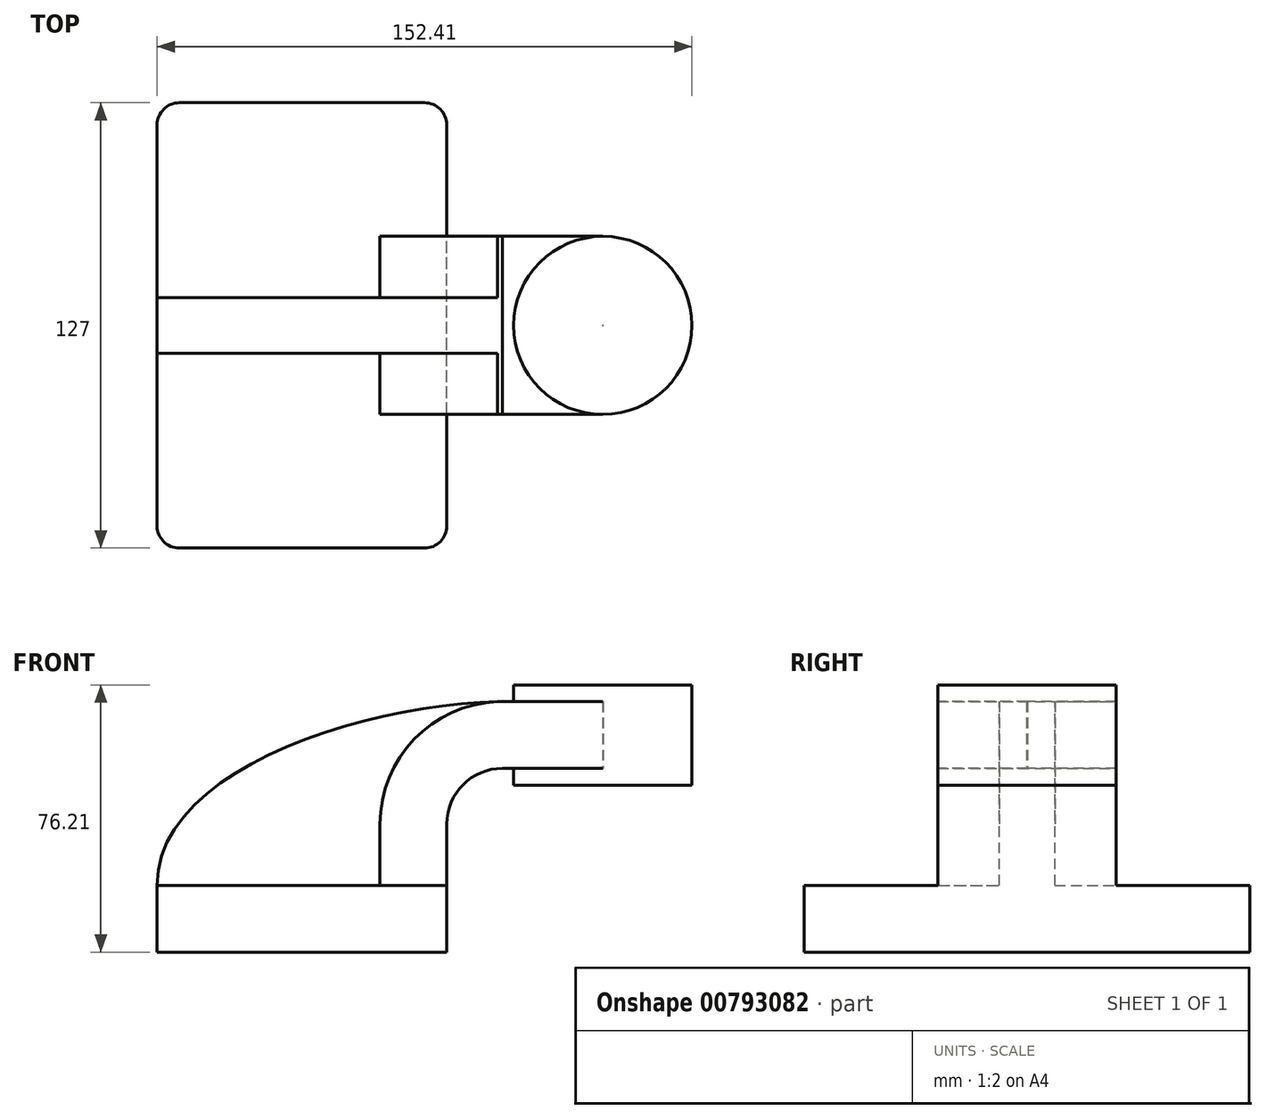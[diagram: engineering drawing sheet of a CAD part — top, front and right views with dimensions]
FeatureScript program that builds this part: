
annotation { "Feature Type Name" : "Feature", "Feature Type Description" : "" }
export const myFeature = defineFeature(function(context is Context, id is Id, definition is map)
    precondition{}
    {
        {
            var Q0;
            Q0=qCreatedBy(makeId("Front.planeOp"),FACE);
            var sketch = newSketch(context, id + "F0", { "sketchPlane" : qUnion([Q0])});
            skLineSegment(sketch, "E0.bottom", {"start": v(-41.28, 9.52) * mm, "end": v(41.27, 9.53) * mm});
            skLineSegment(sketch, "E0.top", {"start": v(-41.28, -9.52) * mm, "end": v(41.28, -9.52) * mm});
            skLineSegment(sketch, "E0.left", {"start": v(-41.28, 9.52) * mm, "end": v(-41.28, -9.53) * mm});
            skLineSegment(sketch, "E0.right", {"start": v(41.27, 9.53) * mm, "end": v(41.28, -9.52) * mm});
            skPoint(sketch, "E0.middle", {"position": v(0, 0) * mm});
            skLineSegment(sketch, "E1.bottom", {"start": v(60.32, 38.1) * mm, "end": v(111.12, 38.1) * mm});
            skLineSegment(sketch, "E1.top", {"start": v(60.32, 66.67) * mm, "end": v(111.12, 66.67) * mm});
            skLineSegment(sketch, "E1.left", {"start": v(60.32, 38.1) * mm, "end": v(60.32, 66.67) * mm});
            skLineSegment(sketch, "E1.right", {"start": v(111.12, 38.1) * mm, "end": v(111.12, 66.67) * mm});
            skPoint(sketch, "E1.middle", {"position": v(85.72, 52.39) * mm});
            skLineSegment(sketch, "E2", {"start": v(41.27, 9.53) * mm, "end": v(41.27, 27) * mm});
            skArc(sketch, "E3", {"start": v(41.27, 27) * mm, "mid": v(45.92, 38.23) * mm, "end": v(57.15, 42.88) * mm});
            skLineSegment(sketch, "E4", {"start": v(57.15, 42.88) * mm, "end": v(85.82, 42.88) * mm});
            skLineSegment(sketch, "E5.0", {"start": v(57.15, 61.93) * mm, "end": v(85.82, 61.93) * mm});
            skArc(sketch, "E5.1", {"start": v(22.22, 27) * mm, "mid": v(32.45, 51.7) * mm, "end": v(57.15, 61.93) * mm});
            skLineSegment(sketch, "E5.2", {"start": v(22.22, 9.53) * mm, "end": v(22.22, 27) * mm});
            skFitSpline(sketch, "E6", {"points": [v(-41.28, 9.52) * mm, v(57.15, 61.93) * mm], "startDerivative": vector(-0.22, 101.04) * mm, "endDerivative": vector(113.45, 1.62) * mm});
            skLineSegment(sketch, "E7", {"start": v(85.82, 42.88) * mm, "end": v(85.82, 61.93) * mm});
            skLineSegment(sketch, "E8", {"start": v(85.72, 38.1) * mm, "end": v(85.72, 66.67) * mm});
            skSolve(sketch);
        }
        {
            var Q0;
            Q0=makeQuery(id+"F0.imprint","IMPRINT",FACE,{"disambiguationData":[TD([[makeQuery(id+"F0.imprint","IMPRINT",EDGE,{"derivedFrom":sQuery(id+"F0.wireOp",EDGE,"E0.top")}),1.0]])]});
            extrude(context, id + "F1", {"entities" : qUnion([Q0]), "endBound" : BoundingType.SYMMETRIC, "depth" : 127 * mm, "offsetDistance" : 25.4 * mm});
        }
        {
            var Q0;
            {var subQ6=sQuery(id+"F0.wireOp",EDGE,"E2");Q0=makeQuery(id+"F0.imprint","IMPRINT",FACE,{"disambiguationData":[TD([[makeQuery(id+"F0.imprint","IMPRINT",EDGE,{"derivedFrom":subQ6}),1.0]])]});}
            var Q1;
            {var subQ0=sQuery(id+"F0.wireOp",EDGE,"E4");var subQ1=sQuery(id+"F0.wireOp",EDGE,"E1.left");var subQ2=makeQuery(id+"F0.imprint","INTERSECT",VERTEX,{"derivedFrom":[subQ1,subQ0]});Q1=makeQuery(id+"F0.imprint","IMPRINT",FACE,{"disambiguationData":[TD([[makeQuery(id+"F0.imprint","IMPRINT",EDGE,{"disambiguationData":[TD([[subQ2,-1.0]])],"derivedFrom":subQ1}),-1.0]])]});}
            extrude(context, id + "F2", {"entities" : qUnion([Q0, Q1]), "operationType" : NewBodyOperationType.ADD, "endBound" : BoundingType.SYMMETRIC, "depth" : 50.8 * mm, "offsetDistance" : 25.4 * mm});
        }
        {
            var Q0;
            {var subQ3=sQuery(id+"F0.wireOp",EDGE,"E5.2");Q0=makeQuery(id+"F0.imprint","IMPRINT",FACE,{"disambiguationData":[TD([[makeQuery(id+"F0.imprint","IMPRINT",EDGE,{"derivedFrom":subQ3}),1.0]])]});}
            extrude(context, id + "F3", {"entities" : qUnion([Q0]), "operationType" : NewBodyOperationType.ADD, "endBound" : BoundingType.SYMMETRIC, "depth" : 15.88 * mm, "offsetDistance" : 25.4 * mm});
        }
        {
            var Q0;
            {var subQ4=sQuery(id+"F0.wireOp",EDGE,"E1.right");Q0=makeQuery(id+"F0.imprint","IMPRINT",FACE,{"disambiguationData":[TD([[makeQuery(id+"F0.imprint","IMPRINT",EDGE,{"derivedFrom":subQ4}),1.0]])]});}
            var Q1;
            Q1=sQuery(id+"F0.wireOp",EDGE,"E8");
            revolve(context, id + "F4", {"operationType" : NewBodyOperationType.ADD, "surfaceOperationType" : NewSurfaceOperationType.NEW, "entities" : qUnion([Q0]), "axis" : qUnion([Q1]), "revolveType" : RevolveType.FULL});
        }
        {
            var Q0;
            Q0=makeQuery(id+"F1.opExtrude","CAP_EDGE",EDGE,{"disambiguationData":[OSD([sQuery(id+"F0.wireOp",EDGE,"E0.left")])],"isStart":false});
            var Q1;
            Q1=makeQuery(id+"F1.opExtrude","CAP_EDGE",EDGE,{"disambiguationData":[OSD([sQuery(id+"F0.wireOp",EDGE,"E0.right")])],"isStart":false});
            var Q2;
            Q2=makeQuery(id+"F1.opExtrude","CAP_EDGE",EDGE,{"disambiguationData":[OSD([sQuery(id+"F0.wireOp",EDGE,"E0.left")])],"isStart":true});
            var Q3;
            Q3=makeQuery(id+"F1.opExtrude","CAP_EDGE",EDGE,{"disambiguationData":[OSD([sQuery(id+"F0.wireOp",EDGE,"E0.right")])],"isStart":true});
            fillet(context, id + "F5", {"entities" : qUnion([Q0, Q1, Q2, Q3]), "radius" : 6.35 * mm, "tangentPropagation" : true, "allowEdgeOverflow" : false});
        }
    });
